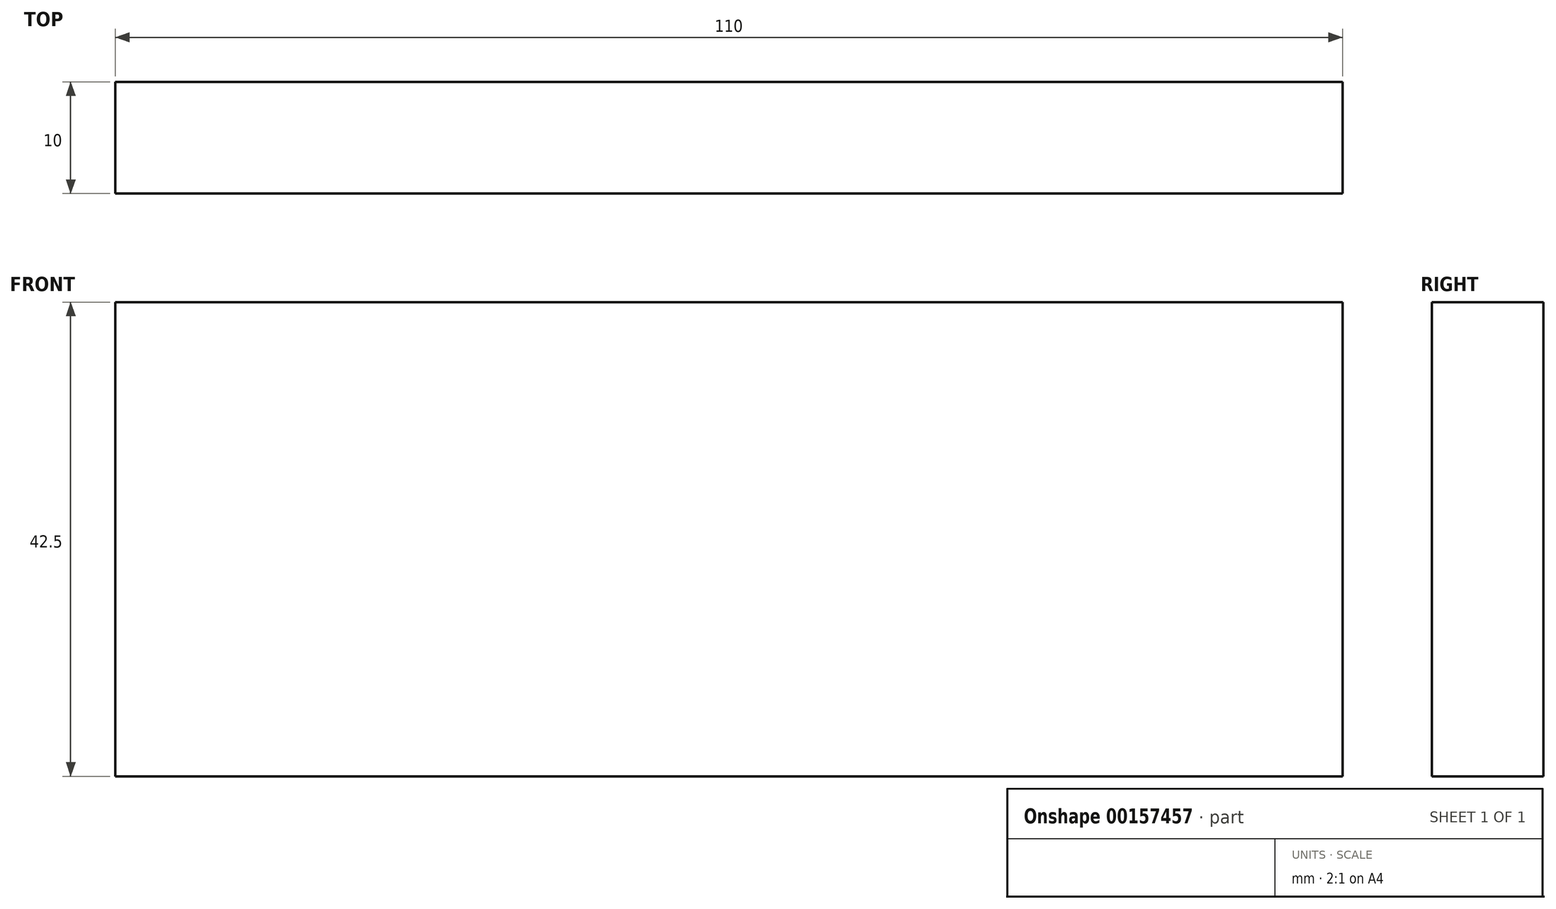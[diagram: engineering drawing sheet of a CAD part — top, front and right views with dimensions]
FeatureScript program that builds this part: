
annotation { "Feature Type Name" : "Feature", "Feature Type Description" : "" }
export const myFeature = defineFeature(function(context is Context, id is Id, definition is map)
    precondition{}
    {
        {
            var Q0;
            Q0=qCreatedBy(makeId("Front.planeOp"),FACE);
            var sketch = newSketch(context, id + "F0", { "sketchPlane" : qUnion([Q0])});
            skLineSegment(sketch, "E0.bottom", {"start": v(55, -21.25) * mm, "end": v(-55, -21.25) * mm});
            skLineSegment(sketch, "E0.top", {"start": v(55, 21.25) * mm, "end": v(-55, 21.25) * mm});
            skLineSegment(sketch, "E0.left", {"start": v(55, -21.25) * mm, "end": v(55, 21.25) * mm});
            skLineSegment(sketch, "E0.right", {"start": v(-55, -21.25) * mm, "end": v(-55, 21.25) * mm});
            skPoint(sketch, "E0.middle", {"position": v(0, 0) * mm});
            skSolve(sketch);
        }
        {
            var Q0;
            Q0=makeQuery(id+"F0.imprint","IMPRINT",FACE,{"disambiguationData":[TD([[makeQuery(id+"F0.imprint","IMPRINT",EDGE,{"derivedFrom":sQuery(id+"F0.wireOp",EDGE,"E0.bottom")}),-1.0]])]});
            extrude(context, id + "F1", {"entities" : qUnion([Q0]), "depth" : 10 * mm});
        }
    });
